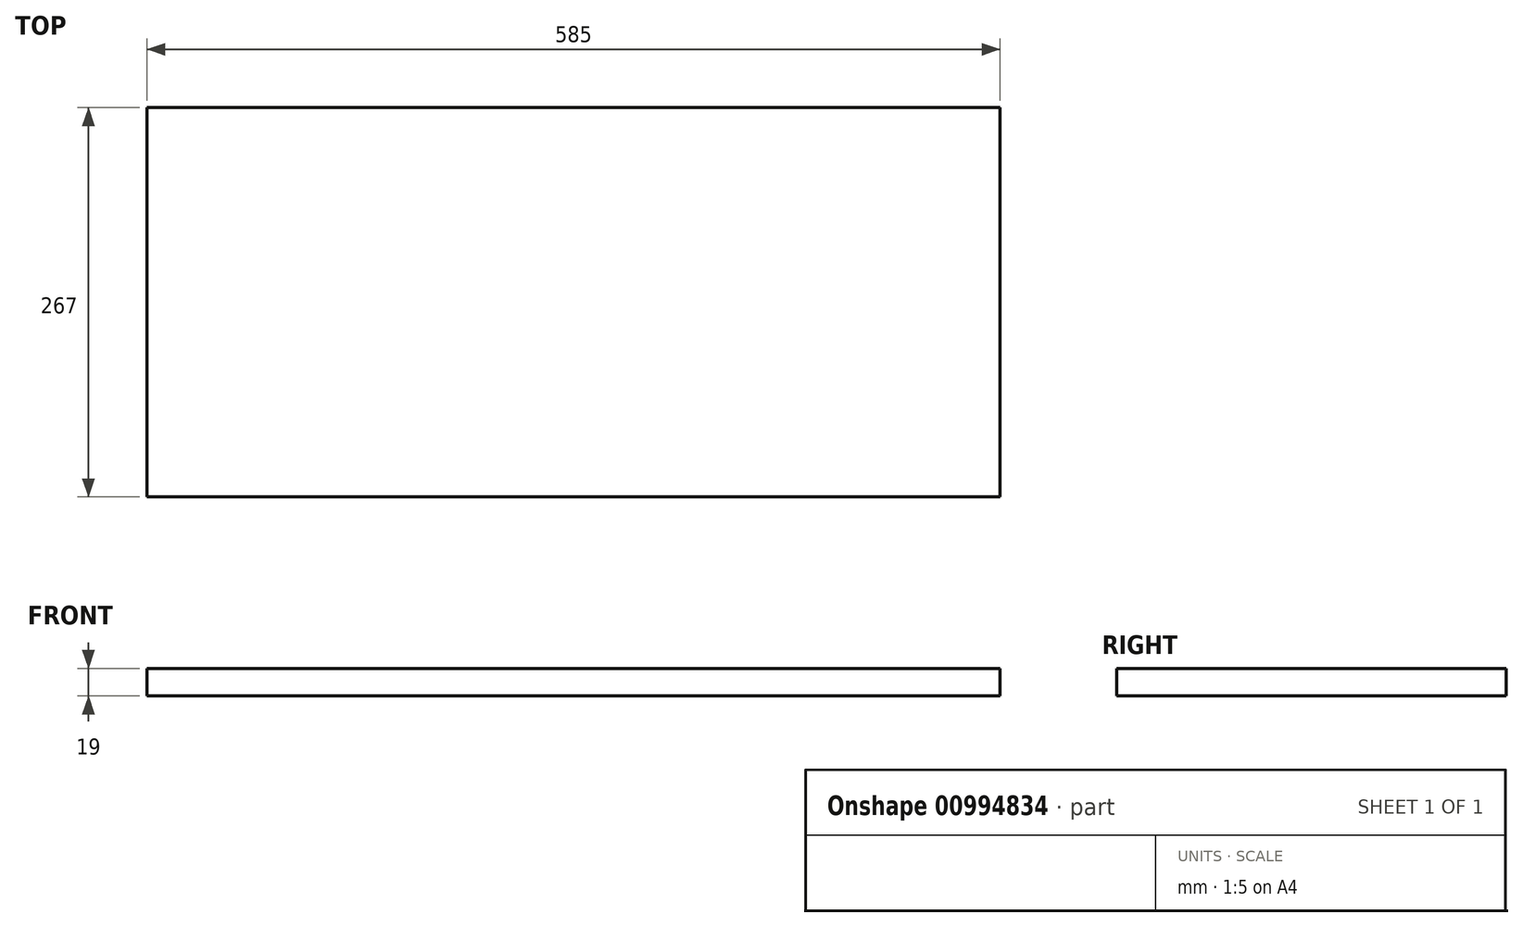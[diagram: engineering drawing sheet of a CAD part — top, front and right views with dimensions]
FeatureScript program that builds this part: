
annotation { "Feature Type Name" : "Feature", "Feature Type Description" : "" }
export const myFeature = defineFeature(function(context is Context, id is Id, definition is map)
    precondition{}
    {
        {
            var Q0;
            Q0=qCreatedBy(makeId("Top.planeOp"),FACE);
            var sketch = newSketch(context, id + "F0", { "sketchPlane" : qUnion([Q0])});
            skLineSegment(sketch, "E0.bottom", {"start": v(0, 0) * mm, "end": v(585, 0) * mm});
            skLineSegment(sketch, "E0.top", {"start": v(0, 267) * mm, "end": v(585, 267) * mm});
            skLineSegment(sketch, "E0.left", {"start": v(0, 0) * mm, "end": v(0, 267) * mm});
            skLineSegment(sketch, "E0.right", {"start": v(585, 0) * mm, "end": v(585, 267) * mm});
            skSolve(sketch);
        }
        {
            var Q0;
            Q0=qSketchRegion(id+"F0",true);
            extrude(context, id + "F1", {"entities" : qUnion([Q0]), "depth" : 19 * mm});
        }
    });
